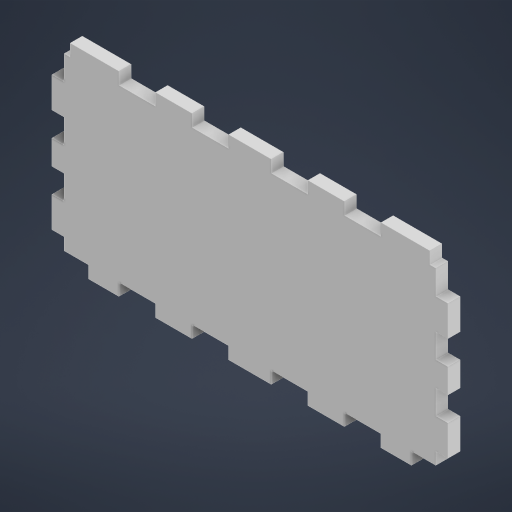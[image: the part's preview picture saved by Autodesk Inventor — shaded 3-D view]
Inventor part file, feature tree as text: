
AUTODESK INVENTOR PART (.ipt)
format: ipt  version: 2023.2 (Build 272271000, 271)  size: 352,256 bytes
history: native  units: mm
features: sketch x2
ambient origin geometry x8: Origin, YZ Plane, XZ Plane, XY Plane, X Axis, Y Axis, Z Axis, Center Point
bodies: Body1 (feature_tree)
feature tree (2):
  sketch  "Sketch1"  dims[d228=130.0mm]
  sketch  "Sketch2"  dims[d229=64.0mm d230=4.0mm d231=0.0mm d234=10.0mm d235=12.0mm d236=12.0mm d237=12.0mm d238=14.0mm d240=12.0mm d242=12.0mm d243=10.0mm d244=12.0mm d245=12.0mm d246=12.0mm d249=8.0mm d251=8.0mm d255=8.0mm d259=4.0mm d260=0.0mm d262=4.0mm d267=8.0mm d268=10.0mm d271=10.0mm d273=6.0mm d275=12.0mm d9=0.5mm d10=0.872665mm d11=0.5mm d12=0.872665mm d13=0.5mm d14=0.872665mm d27=0.5mm d28=0.872665mm d29=0.5mm d30=0.872665mm d88=0.5mm d89=0.872665mm d90=0.5mm d91=0.872665mm d116=0.5mm d117=0.872665mm d118=0.5mm d119=0.872665mm d154=0.5mm d155=0.872665mm d156=0.5mm d157=0.872665mm d181=0.5mm d182=0.872665mm d183=0.5mm d184=0.872665mm d221=0.5mm d222=0.872665mm d223=0.5mm d224=0.872665mm]
